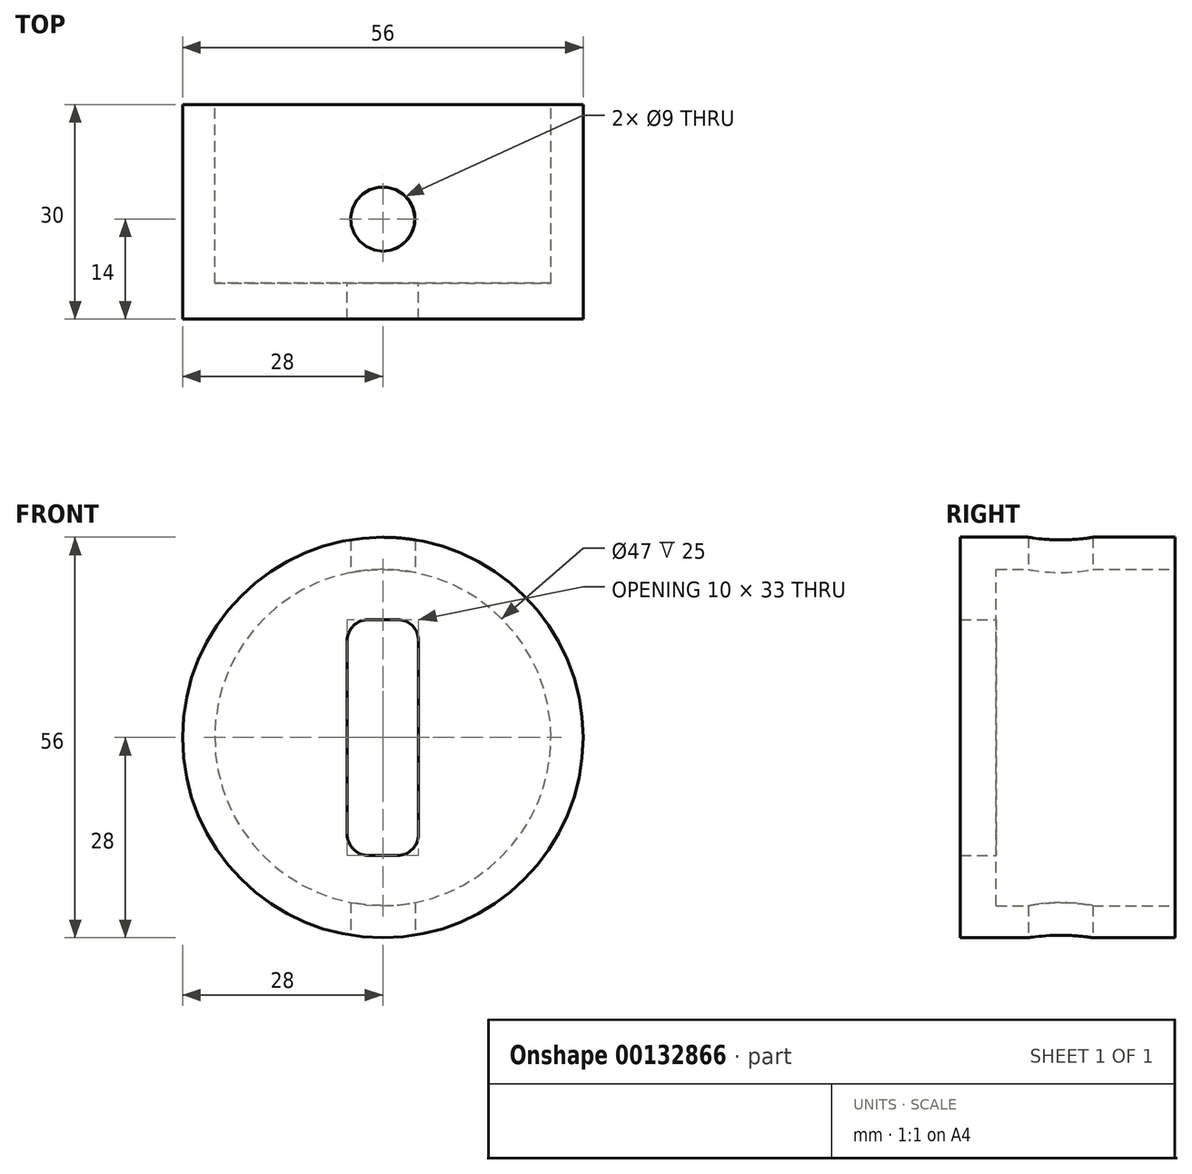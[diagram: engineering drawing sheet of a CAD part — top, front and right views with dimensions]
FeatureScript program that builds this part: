
annotation { "Feature Type Name" : "Feature", "Feature Type Description" : "" }
export const myFeature = defineFeature(function(context is Context, id is Id, definition is map)
    precondition{}
    {
        {
            var Q0;
            Q0=qCreatedBy(makeId("Front.planeOp"),FACE);
            var sketch = newSketch(context, id + "F0", { "sketchPlane" : qUnion([Q0])});
            skCircle(sketch, "E0", {"center": v(0, 0) * mm, "radius": 23.5 * mm});
            skCircle(sketch, "E1", {"center": v(0, 0) * mm, "radius": 28 * mm});
            skSolve(sketch);
        }
        {
            var Q0;
            Q0 = qSketchRegion(id + "F0", true);
            extrude(context, id + "F1", {"entities" : qUnion([Q0]), "depth" : 25 * mm, "offsetDistance" : 25 * mm});
        }
        {
            var Q0;
            Q0=makeQuery(id+"F1.opExtrude","CAP_FACE",FACE,{"disambiguationData":[OSD([sQuery(id+"F0.wireOp",EDGE,"E0"),sQuery(id+"F0.wireOp",EDGE,"E1")])],"isStart":false});
            var sketch = newSketch(context, id + "F2", { "sketchPlane" : qUnion([Q0])});
            skCircle(sketch, "E2", {"center": v(0, 0) * mm, "radius": 28 * mm});
            skLineSegment(sketch, "E3", {"start": v(-5, 13.5) * mm, "end": v(-5, -13.5) * mm});
            skLineSegment(sketch, "E4", {"start": v(5, 13.5) * mm, "end": v(5, -13.5) * mm});
            skLineSegment(sketch, "E5", {"start": v(2, -16.5) * mm, "end": v(-2, -16.5) * mm});
            skLineSegment(sketch, "E6", {"start": v(2, 16.5) * mm, "end": v(-2, 16.5) * mm});
            skPoint(sketch, "E7.visualSharp", {"position": v(-5, 16.5) * mm});
            skArc(sketch, "E7.filletArc", {"start": v(-2, 16.5) * mm, "mid": v(-4.12, 15.62) * mm, "end": v(-5, 13.5) * mm});
            skPoint(sketch, "E8.visualSharp", {"position": v(5, 16.5) * mm});
            skArc(sketch, "E8.filletArc", {"start": v(5, 13.5) * mm, "mid": v(4.12, 15.62) * mm, "end": v(2, 16.5) * mm});
            skPoint(sketch, "E9.visualSharp", {"position": v(-5, -16.5) * mm});
            skArc(sketch, "E9.filletArc", {"start": v(-5, -13.5) * mm, "mid": v(-4.12, -15.62) * mm, "end": v(-2, -16.5) * mm});
            skPoint(sketch, "E10.visualSharp", {"position": v(5, -16.5) * mm});
            skArc(sketch, "E10.filletArc", {"start": v(2, -16.5) * mm, "mid": v(4.12, -15.62) * mm, "end": v(5, -13.5) * mm});
            skSolve(sketch);
        }
        {
            var Q0;
            Q0 = qSketchRegion(id + "F2", true);
            extrude(context, id + "F3", {"entities" : qUnion([Q0]), "operationType" : NewBodyOperationType.ADD, "depth" : 5 * mm, "offsetDistance" : 25 * mm});
        }
        {
            var Q0;
            Q0=makeQuery(id+"F1.opExtrude","CAP_FACE",FACE,{"disambiguationData":[OSD([sQuery(id+"F0.wireOp",EDGE,"E0"),sQuery(id+"F0.wireOp",EDGE,"E1")])],"isStart":true});
            cPlane(context, id + "F4", {"entities" : qUnion([Q0]), "cplaneType" : CPlaneType.OFFSET, "offset" : 15 * mm, "oppositeDirection" : true, "width" : 150 * mm, "height" : 150 * mm});
        }
        {
            var Q0;
            Q0=qCreatedBy(makeId("Top.planeOp"),FACE);
            var sketch = newSketch(context, id + "F5", { "sketchPlane" : qUnion([Q0])});
            skCircle(sketch, "E11", {"center": v(0, -16) * mm, "radius": 4.5 * mm});
            skSolve(sketch);
        }
        {
            var Q0;
            Q0 = qSketchRegion(id + "F5", true);
            extrude(context, id + "F6", {"entities" : qUnion([Q0]), "operationType" : NewBodyOperationType.REMOVE, "depth" : 50 * mm, "hasSecondDirection" : true, "secondDirectionOppositeDirection" : true, "secondDirectionDepth" : 50 * mm});
        }
    });
